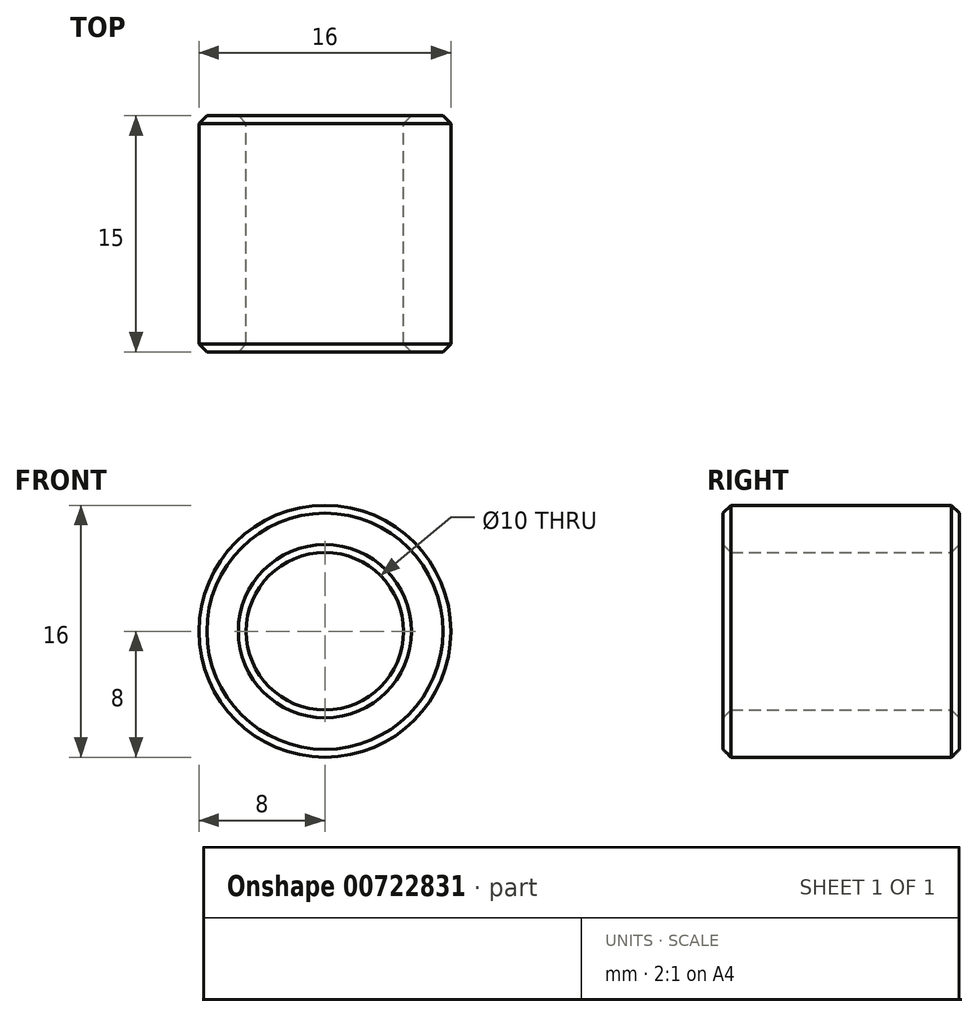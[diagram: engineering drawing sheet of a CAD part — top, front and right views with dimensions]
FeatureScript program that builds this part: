
annotation { "Feature Type Name" : "Feature", "Feature Type Description" : "" }
export const myFeature = defineFeature(function(context is Context, id is Id, definition is map)
    precondition{}
    {
        {
            var Q0;
            Q0=qCreatedBy(makeId("Front.planeOp"),FACE);
            var sketch = newSketch(context, id + "F0", { "sketchPlane" : qUnion([Q0])});
            skCircle(sketch, "E0", {"center": v(0, 0) * mm, "radius": 8 * mm});
            skCircle(sketch, "E1", {"center": v(0, 0) * mm, "radius": 5 * mm});
            skSolve(sketch);
        }
        {
            var Q0;
            Q0 = qSketchRegion(id + "F0", true);
            extrude(context, id + "F1", {"entities" : qUnion([Q0]), "endBound" : BoundingType.SYMMETRIC, "depth" : 15 * mm, "offsetDistance" : 25 * mm});
        }
        {
            var Q0;
            Q0=makeQuery(id+"F1.opExtrude","SWEPT_FACE",FACE,{"disambiguationData":[OSD([sQuery(id+"F0.wireOp",EDGE,"E1")])]});
            var Q1;
            Q1=makeQuery(id+"F1.opExtrude","SWEPT_FACE",FACE,{"disambiguationData":[OSD([sQuery(id+"F0.wireOp",EDGE,"E0")])]});
            chamfer(context, id + "F2", {"entities" : qUnion([Q0, Q1]), "width" : .5 * mm, "tangentPropagation" : true});
        }
    });
